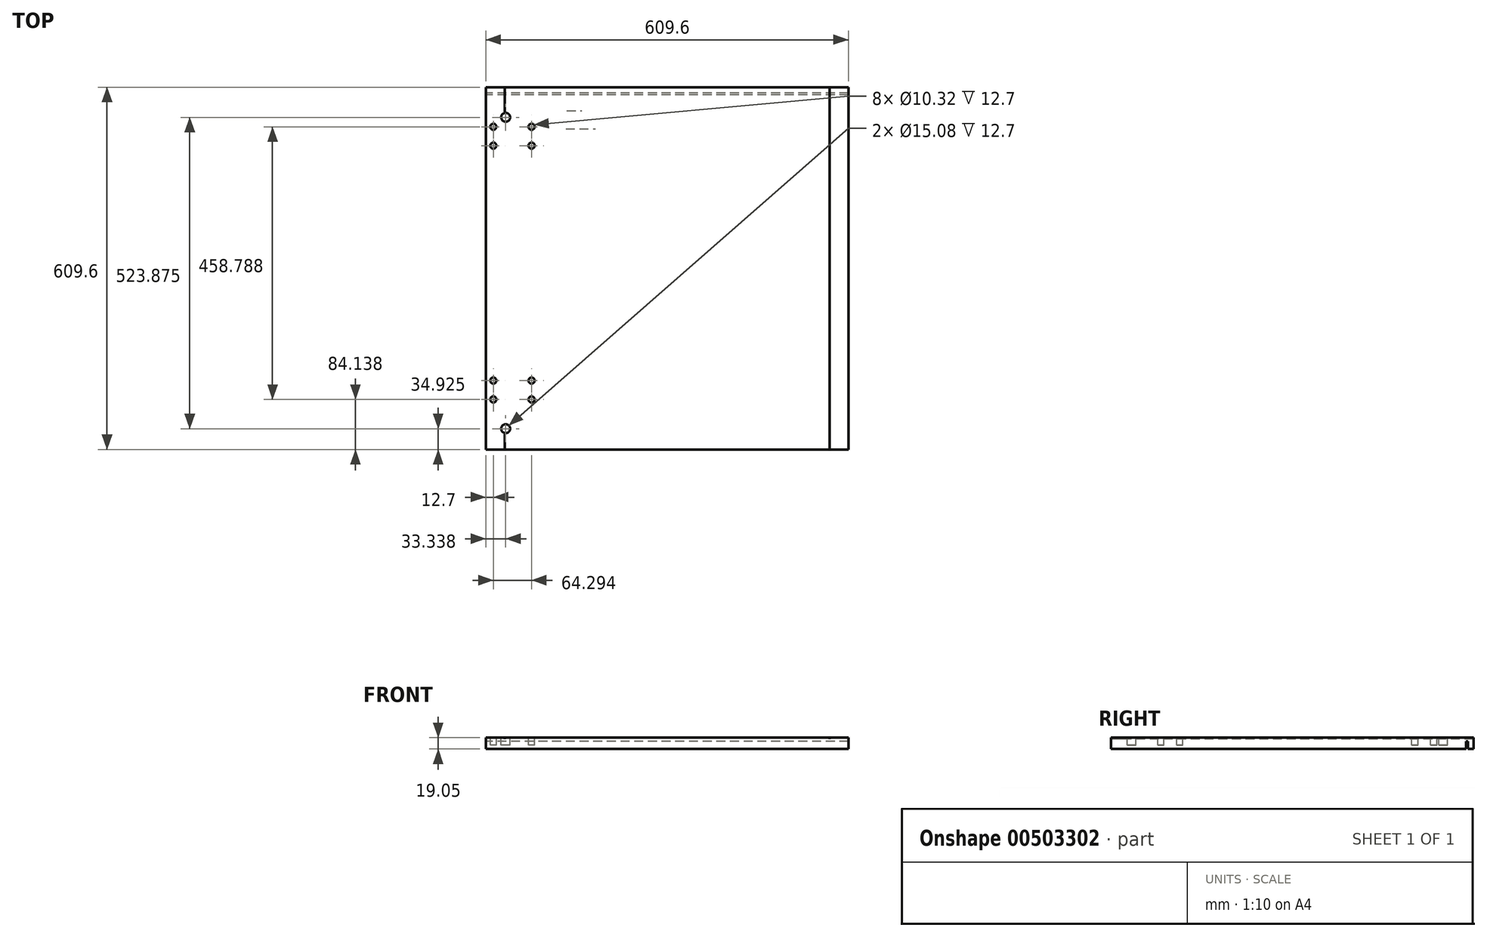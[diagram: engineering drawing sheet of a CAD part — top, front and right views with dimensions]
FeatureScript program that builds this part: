
annotation { "Feature Type Name" : "Feature", "Feature Type Description" : "" }
export const myFeature = defineFeature(function(context is Context, id is Id, definition is map)
    precondition{}
    {
        {
            var Q0;
            Q0=qCreatedBy(makeId("Top.planeOp"),FACE);
            var sketch = newSketch(context, id + "F0", { "sketchPlane" : qUnion([Q0])});
            skLineSegment(sketch, "E0.bottom", {"start": v(-304.8, 304.8) * mm, "end": v(304.8, 304.8) * mm});
            skLineSegment(sketch, "E0.top", {"start": v(-304.8, -304.8) * mm, "end": v(304.8, -304.8) * mm});
            skLineSegment(sketch, "E0.left", {"start": v(-304.8, 304.8) * mm, "end": v(-304.8, -304.8) * mm});
            skLineSegment(sketch, "E0.right", {"start": v(304.8, 304.8) * mm, "end": v(304.8, -304.8) * mm});
            skLineSegment(sketch, "E1", {"start": v(393.38, -304.8) * mm, "end": v(393.38, -188.91) * mm, "construction": true});
            skLineSegment(sketch, "E2", {"start": v(393.38, -188.91) * mm, "end": v(-304.8, -188.91) * mm, "construction": true});
            skLineSegment(sketch, "E3", {"start": v(344.85, -304.8) * mm, "end": v(344.85, -220.66) * mm, "construction": true});
            skLineSegment(sketch, "E4", {"start": v(344.85, -220.66) * mm, "end": v(-304.8, -220.66) * mm, "construction": true});
            skLineSegment(sketch, "E5", {"start": v(321.2, -304.8) * mm, "end": v(321.2, -269.88) * mm, "construction": true});
            skLineSegment(sketch, "E6", {"start": v(321.2, -269.88) * mm, "end": v(-304.8, -269.88) * mm, "construction": true});
            skLineSegment(sketch, "E7", {"start": v(-304.8, 419.45) * mm, "end": v(-227.8, 419.45) * mm, "construction": true});
            skLineSegment(sketch, "E8", {"start": v(-227.8, 419.45) * mm, "end": v(-227.8, -220.66) * mm, "construction": true});
            skPoint(sketch, "E9", {"position": v(-227.8, -188.91) * mm});
            skLineSegment(sketch, "E10", {"start": v(-304.8, 379.03) * mm, "end": v(-292.1, 379.03) * mm, "construction": true});
            skLineSegment(sketch, "E11", {"start": v(-292.1, 379.03) * mm, "end": v(-292.1, -220.66) * mm, "construction": true});
            skPoint(sketch, "E12", {"position": v(-292.1, -188.91) * mm});
            skLineSegment(sketch, "E13", {"start": v(-304.8, 399.62) * mm, "end": v(-271.46, 399.62) * mm, "construction": true});
            skLineSegment(sketch, "E14", {"start": v(-271.46, 399.62) * mm, "end": v(-271.46, -269.88) * mm, "construction": true});
            skCircle(sketch, "E15", {"center": v(-271.46, -269.88) * mm, "radius": 7.54 * mm});
            skCircle(sketch, "E16", {"center": v(-227.8, -220.66) * mm, "radius": 5.16 * mm});
            skCircle(sketch, "E17", {"center": v(-227.8, -188.91) * mm, "radius": 5.16 * mm});
            skCircle(sketch, "E18", {"center": v(-292.1, -188.91) * mm, "radius": 5.16 * mm});
            skCircle(sketch, "E19", {"center": v(-292.1, -220.66) * mm, "radius": 5.16 * mm});
            skLineSegment(sketch, "E20", {"start": v(396.02, 304.8) * mm, "end": v(396.02, 206.37) * mm, "construction": true});
            skLineSegment(sketch, "E21", {"start": v(319.7, 304.8) * mm, "end": v(319.7, 254) * mm, "construction": true});
            skLineSegment(sketch, "E22", {"start": v(353.84, 304.8) * mm, "end": v(353.84, 238.12) * mm, "construction": true});
            skLineSegment(sketch, "E23", {"start": v(319.7, 254) * mm, "end": v(-304.8, 254) * mm, "construction": true});
            skLineSegment(sketch, "E24", {"start": v(353.84, 238.12) * mm, "end": v(-304.8, 238.12) * mm, "construction": true});
            skLineSegment(sketch, "E25", {"start": v(396.02, 206.37) * mm, "end": v(-304.8, 206.38) * mm, "construction": true});
            skPoint(sketch, "E26", {"position": v(-271.46, 254) * mm});
            skPoint(sketch, "E27", {"position": v(-292.1, 238.12) * mm});
            skPoint(sketch, "E28", {"position": v(-292.1, 206.38) * mm});
            skPoint(sketch, "E29", {"position": v(-227.8, 206.38) * mm});
            skPoint(sketch, "E30", {"position": v(-227.8, 238.12) * mm});
            skCircle(sketch, "E31", {"center": v(-271.46, 254) * mm, "radius": 7.54 * mm});
            skCircle(sketch, "E32", {"center": v(-227.8, 238.12) * mm, "radius": 5.16 * mm});
            skCircle(sketch, "E33", {"center": v(-292.1, 238.12) * mm, "radius": 5.16 * mm});
            skCircle(sketch, "E34", {"center": v(-292.1, 206.38) * mm, "radius": 5.16 * mm});
            skCircle(sketch, "E35", {"center": v(-227.8, 206.38) * mm, "radius": 5.16 * mm});
            skPoint(sketch, "E36", {"position": v(0, 304.8) * mm});
            skPoint(sketch, "E37", {"position": v(304.8, 0) * mm});
            skSolve(sketch);
        }
        {
            var Q0;
            {var subQ0=sQuery(id+"F0.wireOp",EDGE,"E34");var subQ1=sQuery(id+"F0.wireOp",EDGE,"E0.left");var subQ2=makeQuery(id+"F0.imprint","INTERSECT",VERTEX,{"disambiguationData":[OD(0.0)],"derivedFrom":[subQ1,subQ0]});Q0=makeQuery(id+"F0.imprint","IMPRINT",FACE,{"disambiguationData":[TD([[makeQuery(id+"F0.imprint","IMPRINT",EDGE,{"disambiguationData":[TD([[subQ2,-1.0]])],"derivedFrom":subQ1}),1.0]])]});}
            var Q1;
            {var subQ10=sQuery(id+"F0.wireOp",EDGE,"E0.bottom");Q1=makeQuery(id+"F0.imprint","IMPRINT",FACE,{"disambiguationData":[TD([[makeQuery(id+"F0.imprint","IMPRINT",EDGE,{"derivedFrom":subQ10}),-1.0]])]});}
            var Q2;
            {var subQ0=sQuery(id+"F0.wireOp",EDGE,"E33");var subQ1=sQuery(id+"F0.wireOp",EDGE,"E31");var subQ2=makeQuery(id+"F0.imprint","INTERSECT",VERTEX,{"disambiguationData":[OD(0.0)],"derivedFrom":[subQ1,subQ0]});Q2=makeQuery(id+"F0.imprint","IMPRINT",FACE,{"disambiguationData":[TD([[makeQuery(id+"F0.imprint","IMPRINT",EDGE,{"disambiguationData":[TD([[subQ2,-1.0]])],"derivedFrom":subQ1}),1.0]])]});}
            var Q3;
            {var subQ0=sQuery(id+"F0.wireOp",EDGE,"E33");var subQ1=sQuery(id+"F0.wireOp",EDGE,"E31");var subQ2=makeQuery(id+"F0.imprint","INTERSECT",VERTEX,{"disambiguationData":[OD(0.0)],"derivedFrom":[subQ1,subQ0]});Q3=makeQuery(id+"F0.imprint","IMPRINT",FACE,{"disambiguationData":[TD([[makeQuery(id+"F0.imprint","IMPRINT",EDGE,{"disambiguationData":[TD([[subQ2,1.0]])],"derivedFrom":subQ1}),1.0]])]});}
            var Q4;
            {var subQ0=sQuery(id+"F0.wireOp",EDGE,"E33");var subQ1=sQuery(id+"F0.wireOp",EDGE,"E0.left");var subQ2=makeQuery(id+"F0.imprint","INTERSECT",VERTEX,{"disambiguationData":[OD(0.0)],"derivedFrom":[subQ1,subQ0]});Q4=makeQuery(id+"F0.imprint","IMPRINT",FACE,{"disambiguationData":[TD([[makeQuery(id+"F0.imprint","IMPRINT",EDGE,{"disambiguationData":[TD([[subQ2,-1.0]])],"derivedFrom":subQ1}),1.0]])]});}
            var Q5;
            Q5=makeQuery(id+"F0.imprint","IMPRINT",FACE,{"disambiguationData":[TD([[makeQuery(id+"F0.imprint","IMPRINT",EDGE,{"derivedFrom":sQuery(id+"F0.wireOp",EDGE,"E35")}),1.0]])]});
            var Q6;
            Q6=makeQuery(id+"F0.imprint","IMPRINT",FACE,{"disambiguationData":[TD([[makeQuery(id+"F0.imprint","IMPRINT",EDGE,{"derivedFrom":sQuery(id+"F0.wireOp",EDGE,"E32")}),1.0]])]});
            var Q7;
            Q7=makeQuery(id+"F0.imprint","IMPRINT",FACE,{"disambiguationData":[TD([[makeQuery(id+"F0.imprint","IMPRINT",EDGE,{"derivedFrom":sQuery(id+"F0.wireOp",EDGE,"E17")}),1.0]])]});
            var Q8;
            Q8=makeQuery(id+"F0.imprint","IMPRINT",FACE,{"disambiguationData":[TD([[makeQuery(id+"F0.imprint","IMPRINT",EDGE,{"derivedFrom":sQuery(id+"F0.wireOp",EDGE,"E16")}),1.0]])]});
            var Q9;
            {var subQ0=sQuery(id+"F0.wireOp",EDGE,"E19");var subQ1=sQuery(id+"F0.wireOp",EDGE,"E0.left");var subQ2=makeQuery(id+"F0.imprint","INTERSECT",VERTEX,{"disambiguationData":[OD(0.0)],"derivedFrom":[subQ1,subQ0]});Q9=makeQuery(id+"F0.imprint","IMPRINT",FACE,{"disambiguationData":[TD([[makeQuery(id+"F0.imprint","IMPRINT",EDGE,{"disambiguationData":[TD([[subQ2,-1.0]])],"derivedFrom":subQ1}),-1.0]])]});}
            var Q10;
            {var subQ0=sQuery(id+"F0.wireOp",EDGE,"E19");var subQ1=sQuery(id+"F0.wireOp",EDGE,"E0.left");var subQ2=makeQuery(id+"F0.imprint","INTERSECT",VERTEX,{"disambiguationData":[OD(0.0)],"derivedFrom":[subQ1,subQ0]});Q10=makeQuery(id+"F0.imprint","IMPRINT",FACE,{"disambiguationData":[TD([[makeQuery(id+"F0.imprint","IMPRINT",EDGE,{"disambiguationData":[TD([[subQ2,-1.0]])],"derivedFrom":subQ1}),1.0]])]});}
            var Q11;
            {var subQ0=sQuery(id+"F0.wireOp",EDGE,"E18");var subQ1=sQuery(id+"F0.wireOp",EDGE,"E0.left");var subQ2=makeQuery(id+"F0.imprint","INTERSECT",VERTEX,{"disambiguationData":[OD(0.0)],"derivedFrom":[subQ1,subQ0]});Q11=makeQuery(id+"F0.imprint","IMPRINT",FACE,{"disambiguationData":[TD([[makeQuery(id+"F0.imprint","IMPRINT",EDGE,{"disambiguationData":[TD([[subQ2,-1.0]])],"derivedFrom":subQ1}),-1.0]])]});}
            var Q12;
            {var subQ0=sQuery(id+"F0.wireOp",EDGE,"E18");var subQ1=sQuery(id+"F0.wireOp",EDGE,"E0.left");var subQ2=makeQuery(id+"F0.imprint","INTERSECT",VERTEX,{"disambiguationData":[OD(0.0)],"derivedFrom":[subQ1,subQ0]});Q12=makeQuery(id+"F0.imprint","IMPRINT",FACE,{"disambiguationData":[TD([[makeQuery(id+"F0.imprint","IMPRINT",EDGE,{"disambiguationData":[TD([[subQ2,-1.0]])],"derivedFrom":subQ1}),1.0]])]});}
            var Q13;
            Q13=makeQuery(id+"F0.imprint","IMPRINT",FACE,{"disambiguationData":[TD([[makeQuery(id+"F0.imprint","IMPRINT",EDGE,{"derivedFrom":sQuery(id+"F0.wireOp",EDGE,"E15")}),1.0]])]});
            var Q14;
            Q14=makeQuery(id+"F0.imprint","IMPRINT",FACE,{"disambiguationData":[TD([[makeQuery(id+"F0.imprint","IMPRINT",EDGE,{"derivedFrom":sQuery(id+"F0.wireOp",EDGE,"E31")}),1.0]])]});
            var Q15;
            Q15=makeQuery(id+"F0.imprint","IMPRINT",FACE,{"disambiguationData":[TD([[makeQuery(id+"F0.imprint","IMPRINT",EDGE,{"derivedFrom":sQuery(id+"F0.wireOp",EDGE,"E33")}),1.0]])]});
            var Q16;
            Q16=makeQuery(id+"F0.imprint","IMPRINT",FACE,{"disambiguationData":[TD([[makeQuery(id+"F0.imprint","IMPRINT",EDGE,{"derivedFrom":sQuery(id+"F0.wireOp",EDGE,"E34")}),1.0]])]});
            var Q17;
            Q17=makeQuery(id+"F0.imprint","IMPRINT",FACE,{"disambiguationData":[TD([[makeQuery(id+"F0.imprint","IMPRINT",EDGE,{"derivedFrom":sQuery(id+"F0.wireOp",EDGE,"E19")}),1.0]])]});
            var Q18;
            Q18=makeQuery(id+"F0.imprint","IMPRINT",FACE,{"disambiguationData":[TD([[makeQuery(id+"F0.imprint","IMPRINT",EDGE,{"derivedFrom":sQuery(id+"F0.wireOp",EDGE,"E18")}),1.0]])]});
            extrude(context, id + "F1", {"entities" : qUnion([Q0, Q1, Q2, Q3, Q4, Q5, Q6, Q7, Q8, Q9, Q10, Q11, Q12, Q13, Q14, Q15, Q16, Q17, Q18]), "oppositeDirection" : true, "depth" : 19.05 * mm});
        }
        {
            var Q0;
            Q0=makeQuery(id+"F0.imprint","IMPRINT",FACE,{"disambiguationData":[TD([[makeQuery(id+"F0.imprint","IMPRINT",EDGE,{"derivedFrom":sQuery(id+"F0.wireOp",EDGE,"E15")}),1.0]])]});
            var Q1;
            Q1=makeQuery(id+"F0.imprint","IMPRINT",FACE,{"disambiguationData":[TD([[makeQuery(id+"F0.imprint","IMPRINT",EDGE,{"derivedFrom":sQuery(id+"F0.wireOp",EDGE,"E19")}),1.0]])]});
            var Q2;
            Q2=makeQuery(id+"F0.imprint","IMPRINT",FACE,{"disambiguationData":[TD([[makeQuery(id+"F0.imprint","IMPRINT",EDGE,{"derivedFrom":sQuery(id+"F0.wireOp",EDGE,"E16")}),1.0]])]});
            var Q3;
            Q3=makeQuery(id+"F0.imprint","IMPRINT",FACE,{"disambiguationData":[TD([[makeQuery(id+"F0.imprint","IMPRINT",EDGE,{"derivedFrom":sQuery(id+"F0.wireOp",EDGE,"E17")}),1.0]])]});
            var Q4;
            Q4=makeQuery(id+"F0.imprint","IMPRINT",FACE,{"disambiguationData":[TD([[makeQuery(id+"F0.imprint","IMPRINT",EDGE,{"derivedFrom":sQuery(id+"F0.wireOp",EDGE,"E18")}),1.0]])]});
            var Q5;
            Q5=makeQuery(id+"F0.imprint","IMPRINT",FACE,{"disambiguationData":[TD([[makeQuery(id+"F0.imprint","IMPRINT",EDGE,{"derivedFrom":sQuery(id+"F0.wireOp",EDGE,"E34")}),1.0]])]});
            var Q6;
            Q6=makeQuery(id+"F0.imprint","IMPRINT",FACE,{"disambiguationData":[TD([[makeQuery(id+"F0.imprint","IMPRINT",EDGE,{"derivedFrom":sQuery(id+"F0.wireOp",EDGE,"E35")}),1.0]])]});
            var Q7;
            Q7=makeQuery(id+"F0.imprint","IMPRINT",FACE,{"disambiguationData":[TD([[makeQuery(id+"F0.imprint","IMPRINT",EDGE,{"derivedFrom":sQuery(id+"F0.wireOp",EDGE,"E32")}),1.0]])]});
            var Q8;
            Q8=makeQuery(id+"F0.imprint","IMPRINT",FACE,{"disambiguationData":[TD([[makeQuery(id+"F0.imprint","IMPRINT",EDGE,{"derivedFrom":sQuery(id+"F0.wireOp",EDGE,"E33")}),1.0]])]});
            var Q9;
            Q9=makeQuery(id+"F0.imprint","IMPRINT",FACE,{"disambiguationData":[TD([[makeQuery(id+"F0.imprint","IMPRINT",EDGE,{"derivedFrom":sQuery(id+"F0.wireOp",EDGE,"E31")}),1.0]])]});
            extrude(context, id + "F2", {"entities" : qUnion([Q0, Q1, Q2, Q3, Q4, Q5, Q6, Q7, Q8, Q9]), "operationType" : NewBodyOperationType.REMOVE, "oppositeDirection" : true, "depth" : 12.7 * mm});
        }
        {
            var Q0;
            Q0=makeQuery(id+"F1.opExtrude","CAP_FACE",FACE,{"disambiguationData":[OSD([sQuery(id+"F0.wireOp",EDGE,"E0.bottom"),sQuery(id+"F0.wireOp",EDGE,"E0.top"),sQuery(id+"F0.wireOp",EDGE,"E0.left"),sQuery(id+"F0.wireOp",EDGE,"E0.right")])],"isStart":false});
            var sketch = newSketch(context, id + "F3", { "sketchPlane" : qUnion([Q0])});
            skLineSegment(sketch, "E38", {"start": v(176.5, -304.8) * mm, "end": v(176.5, -295.28) * mm, "construction": true});
            skLineSegment(sketch, "E39.bottom", {"start": v(304.8, -295.28) * mm, "end": v(-304.8, -295.28) * mm});
            skLineSegment(sketch, "E39.top", {"start": v(304.8, -292.1) * mm, "end": v(-304.8, -292.1) * mm});
            skLineSegment(sketch, "E39.left", {"start": v(304.8, -295.28) * mm, "end": v(304.8, -292.1) * mm});
            skLineSegment(sketch, "E39.right", {"start": v(-304.8, -295.28) * mm, "end": v(-304.8, -292.1) * mm});
            skSolve(sketch);
        }
        {
            var Q0;
            Q0=makeQuery(id+"F3.imprint","IMPRINT",FACE,{"disambiguationData":[TD([[makeQuery(id+"F3.imprint","IMPRINT",EDGE,{"derivedFrom":sQuery(id+"F3.wireOp",EDGE,"E39.bottom")}),-1.0]])]});
            extrude(context, id + "F4", {"entities" : qUnion([Q0]), "operationType" : NewBodyOperationType.REMOVE, "oppositeDirection" : true, "depth" : 12.7 * mm});
        }
        {
            var Q0;
            {var subQ0=sQuery(id+"F0.wireOp",EDGE,"E0.top");var subQ1=sQuery(id+"F0.wireOp",EDGE,"E0.left");var subQ2=sQuery(id+"F0.wireOp",EDGE,"E0.right");Q0=makeQuery(id+"F4.boolean.opBoolean","SPLIT",FACE,{"disambiguationData":[TD([makeQuery(id+"F1.opExtrude","SWEPT_FACE",FACE,{"disambiguationData":[OSD([subQ0])]})])],"derivedFrom":makeQuery(id+"F1.opExtrude","CAP_FACE",FACE,{"disambiguationData":[OSD([sQuery(id+"F0.wireOp",EDGE,"E0.bottom"),subQ0,subQ1,subQ2])],"isStart":false})});}
            var sketch = newSketch(context, id + "F5", { "sketchPlane" : qUnion([Q0])});
            skLineSegment(sketch, "E40.bottom", {"start": v(-168.75, -265.08) * mm, "end": v(-143.35, -265.08) * mm});
            skLineSegment(sketch, "E40.top", {"start": v(-168.75, -265.06) * mm, "end": v(-143.35, -265.06) * mm});
            skLineSegment(sketch, "E40.left", {"start": v(-168.75, -265.08) * mm, "end": v(-168.75, -265.06) * mm});
            skLineSegment(sketch, "E40.right", {"start": v(-143.35, -265.08) * mm, "end": v(-143.35, -265.06) * mm});
            skLineSegment(sketch, "E41.bottom", {"start": v(-170.19, -234.87) * mm, "end": v(-120.19, -234.87) * mm});
            skLineSegment(sketch, "E41.top", {"start": v(-170.19, -234.9) * mm, "end": v(-120.19, -234.9) * mm});
            skLineSegment(sketch, "E41.left", {"start": v(-170.19, -234.87) * mm, "end": v(-170.19, -234.9) * mm});
            skLineSegment(sketch, "E41.right", {"start": v(-120.19, -234.87) * mm, "end": v(-120.19, -234.9) * mm});
            skSolve(sketch);
        }
        {
            var Q0;
            Q0=makeQuery(id+"F5.imprint","IMPRINT",FACE,{"disambiguationData":[TD([[makeQuery(id+"F5.imprint","IMPRINT",EDGE,{"derivedFrom":sQuery(id+"F5.wireOp",EDGE,"E40.bottom")}),1.0]])]});
            var Q1;
            Q1=makeQuery(id+"F5.imprint","IMPRINT",FACE,{"disambiguationData":[TD([[makeQuery(id+"F5.imprint","IMPRINT",EDGE,{"derivedFrom":sQuery(id+"F5.wireOp",EDGE,"E41.bottom")}),-1.0]])]});
            extrude(context, id + "F6", {"entities" : qUnion([Q0, Q1]), "operationType" : NewBodyOperationType.REMOVE, "oppositeDirection" : true, "depth" : 0.25 * mm});
        }
        {
            var Q0;
            Q0=makeQuery(id+"F1.opExtrude","CAP_FACE",FACE,{"disambiguationData":[OSD([sQuery(id+"F0.wireOp",EDGE,"E0.bottom"),sQuery(id+"F0.wireOp",EDGE,"E0.top"),sQuery(id+"F0.wireOp",EDGE,"E0.left"),sQuery(id+"F0.wireOp",EDGE,"E0.right")])],"isStart":true});
            var sketch = newSketch(context, id + "F7", { "sketchPlane" : qUnion([Q0])});
            skLineSegment(sketch, "E42", {"start": v(-304.8, 8.16) * mm, "end": v(-273.05, 8.16) * mm, "construction": true});
            skLineSegment(sketch, "E43.bottom", {"start": v(-273.05, 304.8) * mm, "end": v(-273.02, 304.8) * mm});
            skLineSegment(sketch, "E43.top", {"start": v(-273.05, -304.8) * mm, "end": v(-273.02, -304.8) * mm});
            skLineSegment(sketch, "E43.left", {"start": v(-273.05, 304.8) * mm, "end": v(-273.05, -304.8) * mm});
            skLineSegment(sketch, "E43.right", {"start": v(-273.02, 304.8) * mm, "end": v(-273.02, -304.8) * mm});
            skLineSegment(sketch, "E44.MirrorCS", {"start": v(273.05, 304.8) * mm, "end": v(273.05, -304.8) * mm});
            skLineSegment(sketch, "E45.MirrorCS", {"start": v(273.05, -304.8) * mm, "end": v(273.02, -304.8) * mm});
            skLineSegment(sketch, "E46.MirrorCS", {"start": v(273.02, 304.8) * mm, "end": v(273.02, -304.8) * mm});
            skLineSegment(sketch, "E47.MirrorCS", {"start": v(273.05, 304.8) * mm, "end": v(273.02, 304.8) * mm});
            skSolve(sketch);
        }
        {
            var Q0;
            Q0=makeQuery(id+"F7.imprint","IMPRINT",FACE,{"disambiguationData":[TD([[makeQuery(id+"F7.imprint","IMPRINT",EDGE,{"derivedFrom":sQuery(id+"F7.wireOp",EDGE,"E44.MirrorCS")}),-1.0]])]});
            var Q1;
            Q1=makeQuery(id+"F7.imprint","IMPRINT",FACE,{"disambiguationData":[TD([[makeQuery(id+"F7.imprint","IMPRINT",EDGE,{"derivedFrom":sQuery(id+"F7.wireOp",EDGE,"E43.bottom")}),-1.0]])]});
            var Q2;
            {var subQ0=sQuery(id+"F7.wireOp",EDGE,"E43.left");var subQ1=makeQuery(id+"F2.boolean.opBoolean","COPY",EDGE,{"derivedFrom":makeQuery(id+"F2.opExtrude","CAP_EDGE",EDGE,{"disambiguationData":[OSD([sQuery(id+"F0.wireOp",EDGE,"E31")])],"isStart":true})});var subQ2=makeQuery(id+"F7.imprint","INTERSECT",VERTEX,{"disambiguationData":[OD(0.0)],"derivedFrom":[subQ1,subQ0]});Q2=makeQuery(id+"F7.imprint","IMPRINT",FACE,{"disambiguationData":[TD([[makeQuery(id+"F7.imprint","IMPRINT",EDGE,{"disambiguationData":[TD([[subQ2,-1.0]])],"derivedFrom":subQ0}),1.0]])]});}
            var Q3;
            {var subQ0=sQuery(id+"F7.wireOp",EDGE,"E43.left");var subQ1=makeQuery(id+"F2.boolean.opBoolean","COPY",EDGE,{"derivedFrom":makeQuery(id+"F2.opExtrude","CAP_EDGE",EDGE,{"disambiguationData":[OSD([sQuery(id+"F0.wireOp",EDGE,"E15")])],"isStart":true})});var subQ2=makeQuery(id+"F7.imprint","INTERSECT",VERTEX,{"disambiguationData":[OD(0.0)],"derivedFrom":[subQ1,subQ0]});Q3=makeQuery(id+"F7.imprint","IMPRINT",FACE,{"disambiguationData":[TD([[makeQuery(id+"F7.imprint","IMPRINT",EDGE,{"disambiguationData":[TD([[subQ2,-1.0]])],"derivedFrom":subQ0}),1.0]])]});}
            var Q4;
            {var subQ0=sQuery(id+"F7.wireOp",EDGE,"E43.top");Q4=makeQuery(id+"F7.imprint","IMPRINT",FACE,{"disambiguationData":[TD([[makeQuery(id+"F7.imprint","IMPRINT",EDGE,{"derivedFrom":subQ0}),1.0]])]});}
            var Q5;
            {var subQ0=sQuery(id+"F7.wireOp",EDGE,"E43.left");var subQ1=makeQuery(id+"F2.boolean.opBoolean","COPY",EDGE,{"derivedFrom":makeQuery(id+"F2.opExtrude","CAP_EDGE",EDGE,{"disambiguationData":[OSD([sQuery(id+"F0.wireOp",EDGE,"E31")])],"isStart":true})});var subQ2=makeQuery(id+"F7.imprint","INTERSECT",VERTEX,{"disambiguationData":[OD(1.0)],"derivedFrom":[subQ1,subQ0]});Q5=makeQuery(id+"F7.imprint","IMPRINT",FACE,{"disambiguationData":[TD([[makeQuery(id+"F7.imprint","IMPRINT",EDGE,{"disambiguationData":[TD([[subQ2,-1.0]])],"derivedFrom":subQ0}),1.0]])]});}
            extrude(context, id + "F8", {"entities" : qUnion([Q0, Q1, Q2, Q3, Q4, Q5]), "operationType" : NewBodyOperationType.REMOVE, "oppositeDirection" : true, "depth" : 2.54 * mm});
        }
    });
